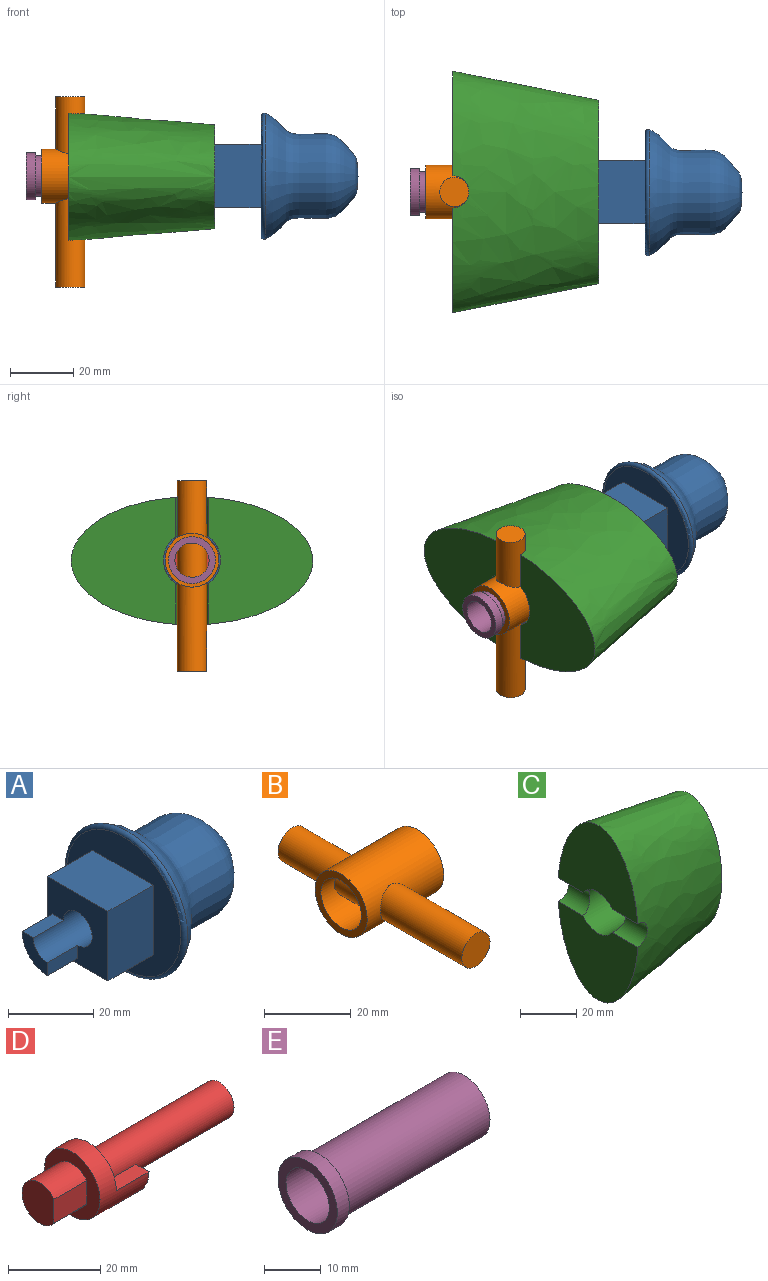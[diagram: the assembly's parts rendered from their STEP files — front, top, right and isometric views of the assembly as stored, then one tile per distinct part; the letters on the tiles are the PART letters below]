
ASSEMBLY  parts=5 mates=4
PART A: 14 faces, bbox 40x43.1x43.1 mm
  f0: plane 10x3.75mm, normal (0,-1,0), area 37.5mm2, adj f2,f3,f8,f11
  f1: plane 10x3.75mm, normal (0,0,1), area 37.5mm2, adj f2,f3,f8,f11
  f2: cylinder r=8.5mm len=10mm, axis (-1,0,0), area 133.5mm2, adj f0,f1,f3,f8
  f3: plane 8.5x8.5mm, normal (-1,0,0), area 39mm2, adj f0,f1,f2,f11
  f4: plane 20x15mm, normal (0,-1,0), area 300mm2, adj f5,f7,f8,f10
  f5: plane 20x15mm, normal (0,0,-1), area 300mm2, adj f4,f6,f8,f10
  f6: plane 20x15mm, normal (0,1,0), area 300mm2, adj f5,f7,f8,f10
  f7: plane 20x15mm, normal (0,0,1), area 300mm2, adj f4,f6,f8,f10
  f8: plane 20x20mm, normal (-1,0,0), area 290.1mm2, adj f0,f1,f2,f4,f5,f6,f7,f11
  f9: revolved ~19.84x19.84mm, area 0mm2, adj f13
  f10: plane 37.83x37.83mm, normal (-1,0,0), area 724.3mm2, adj f4,f5,f6,f7,f13
  f11: cylinder r=4.75mm len=40mm, axis (-1,0,0), area 970mm2, adj f0,f1,f3,f8,f12
  f12: plane 9.5x9.5mm, normal (-1,0,0), area 70.9mm2, adj f11
  f13: torus R=18.92mm, axis (-1,0,0), area 241.2mm2, adj f9,f10
PART B: 9 faces, bbox 25x60x17 mm
  f0: cylinder r=4.6mm len=27.85mm, axis (0,1,0), area 785mm2, adj f1,f3
  f1: plane 9.2x9.2mm, normal (0,-1,0), area 66.5mm2, adj f0
  f2: cylinder r=6.6mm len=25mm, axis (-1,0,0), area 893.7mm2, adj f4,f5,f8
  f3: cylinder r=8.5mm len=25mm, axis (-1,0,0), area 1196.9mm2, adj f0,f4,f5,f7
  f4: plane 17x17mm, normal (1,0,0), area 90.1mm2, adj f2,f3
  f5: plane 17x17mm, normal (-1,0,0), area 90.1mm2, adj f2,f3
  f6: plane 9.2x9.2mm, normal (0,1,0), area 66.5mm2, adj f7
  f7: cylinder r=4.6mm len=17.85mm, axis (0,1,0), area 496mm2, adj f3,f6
  f8: cylinder r=4.6mm len=13.2mm, axis (0,1,0), area 329.8mm2, adj f2
PART C: 12 faces, bbox 46x40.5x76.2 mm
  f0: plane 40.15x33.01mm, normal (-1,0,0), area 964.7mm2, adj f2,f9,f10,f11
  f1: plane 40.15x33.01mm, normal (-1,0,0), area 964.6mm2, adj f2,f9,f10,f11
  f2: bspline ~76.1x46mm, area 7630.9mm2, adj f0,f1,f3,f9,f10
  f3: plane 57.85x32.79mm, normal (1,0,0), area 1089.6mm2, adj f2,f5,f6,f7,f8
  f4: plane 20x20mm, normal (1,0,0), area 145.5mm2, adj f5,f6,f7,f8,f11
  f5: plane 30x20mm, normal (0,0,-1), area 600mm2, adj f3,f4,f6,f8
  f6: plane 30x20mm, normal (0,1,0), area 600mm2, adj f3,f4,f5,f7
  f7: plane 30x20mm, normal (0,0,1), area 600mm2, adj f3,f4,f6,f8
  f8: plane 30x20mm, normal (0,-1,0), area 600mm2, adj f3,f4,f5,f7
  f9: cylinder r=5.1mm len=12.44mm, axis (0,1,0), area 183.5mm2, adj f0,f1,f2,f11
  f10: cylinder r=5.1mm len=12.84mm, axis (0,1,0), area 189.9mm2, adj f0,f1,f2,f11
  f11: cylinder r=9mm len=18mm, axis (-1,0,0), area 819.3mm2, adj f0,f1,f4,f9,f10
PART D: 11 faces, bbox 55x17x17 mm
  f0: cylinder r=4.5mm len=40mm, axis (-1,0,0), area 1060.3mm2, adj f6,f7,f8,f9,f10
  f1: cylinder r=5.39mm len=10.78mm, axis (1,0,0), area 271.9mm2, adj f2,f3,f4
  f2: plane 10x6.25mm, normal (0,-1,0), area 62.5mm2, adj f1,f3,f4
  f3: plane 10.78x9.78mm, normal (-1,0,0), area 87mm2, adj f1,f2
  f4: plane 17x17mm, normal (-1,0,0), area 140mm2, adj f1,f2,f5
  f5: cylinder r=8.5mm len=17mm, axis (-1,0,0), area 400.6mm2, adj f4,f6,f8,f9,f10
  f6: plane 17x17mm, normal (1,0,0), area 122.5mm2, adj f0,f5,f8,f9
  f7: plane 9x9mm, normal (1,0,0), area 63.6mm2, adj f0
  f8: plane 10x4mm, normal (0,1,0), area 40mm2, adj f0,f5,f6,f10
  f9: plane 10x4mm, normal (0,0,1), area 40mm2, adj f0,f5,f6,f10
  f10: plane 8.5x8.5mm, normal (1,0,0), area 40.8mm2, adj f0,f5,f8,f9
PART E: 8 faces, bbox 39x14.8x14.8 mm
  f0: cylinder r=6.39mm len=36mm, axis (-1,0,0), area 1445.4mm2, adj f1,f5
  f1: plane 12.78x12.78mm, normal (1,0,0), area 41.3mm2, adj f0,f2,f6
  f2: cylinder r=5.39mm len=39mm, axis (-1,0,0), area 1154mm2, adj f1,f3,f6,f7
  f3: plane 14.78x14.78mm, normal (-1,0,0), area 80.3mm2, adj f2,f4
  f4: cylinder r=7.39mm len=14.78mm, axis (-1,0,0), area 139.3mm2, adj f3,f5
  f5: plane 14.78x14.78mm, normal (1,0,0), area 43.3mm2, adj f0,f4
  f6: plane 25x6.25mm, normal (0,1,0), area 156.4mm2, adj f1,f2,f7
  f7: plane 6.25x1mm, normal (-1,0,0), area 4.3mm2, adj f2,f6
PLACE A t=(168.84,-14.33,-3.62)mm
PLACE B rot(axis=(1,0,0),90deg) t=(154.64,-39.33,21.38)mm
PLACE C rot(axis=(1,0,0),90deg) t=(154.14,-39.33,21.38)mm
PLACE D rot(axis=(1,0,0),90deg) t=(163.64,-39.33,21.38)mm
PLACE E rot(axis=(1,0,0),90deg) t=(163.64,-39.33,21.38)mm
MATE fastened B.f3 <-> C.f11  axis (-1,0,0) through (158.14,-39.33,-3.62)mm
MATE slider E.f2 <-> B.f3  axis (1,0,0) through (179.64,-39.33,-3.62)mm
MATE fastened D.f5 <-> E.f2  axis (-1,0,0) through (179.64,-39.33,-3.62)mm
MATE cylindrical A.f11 <-> D.f0  axis (-1,0,0) through (199.84,-39.33,-3.62)mm
